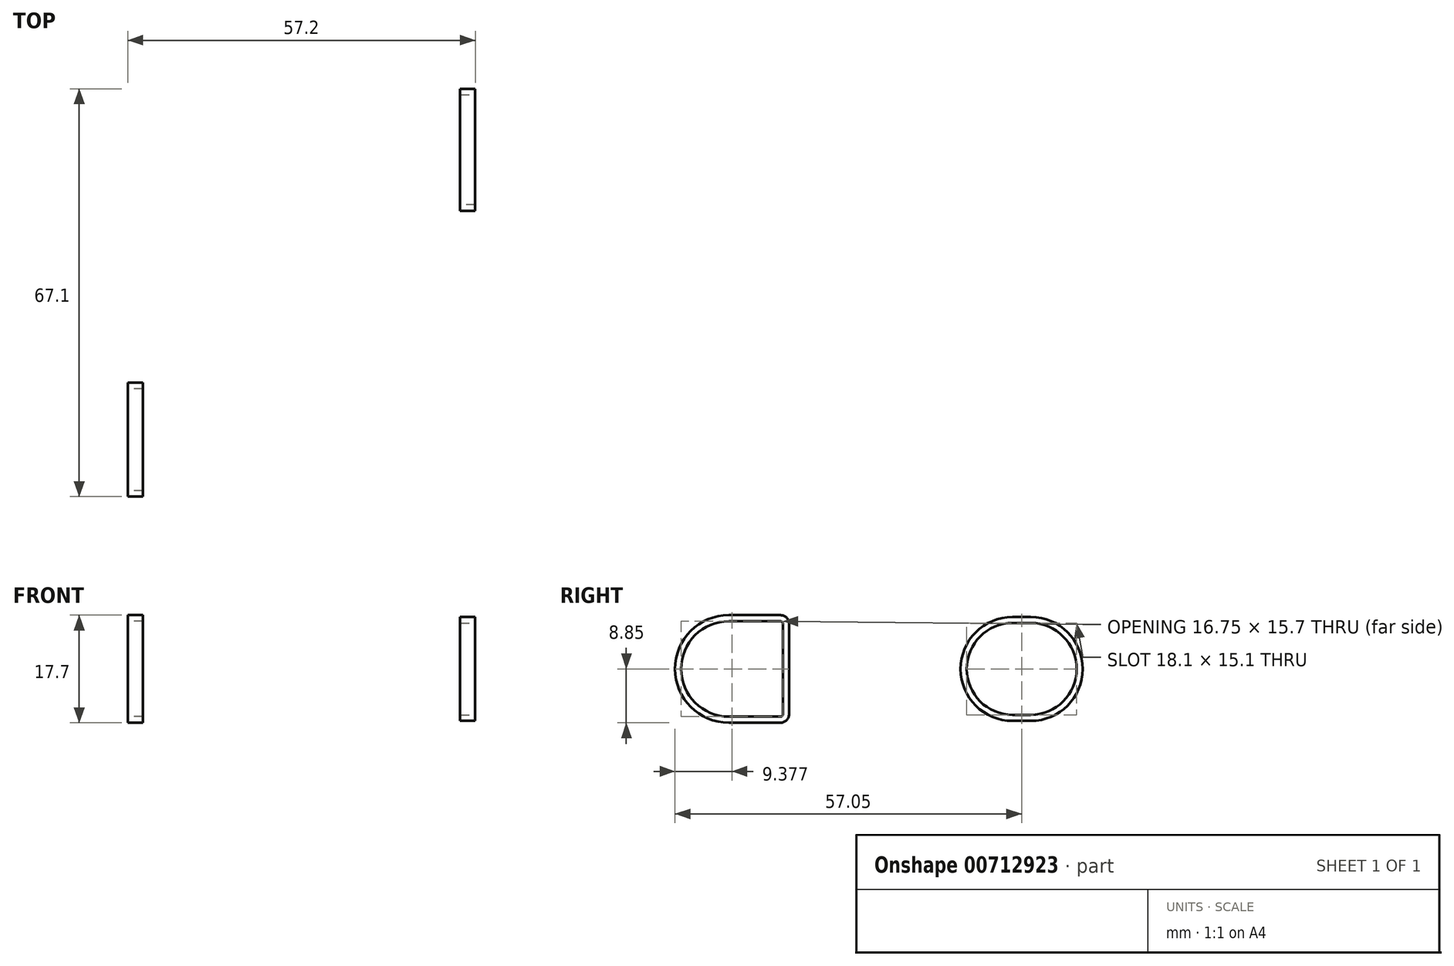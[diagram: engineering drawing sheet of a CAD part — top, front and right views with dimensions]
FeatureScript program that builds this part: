
annotation { "Feature Type Name" : "Feature", "Feature Type Description" : "" }
export const myFeature = defineFeature(function(context is Context, id is Id, definition is map)
    precondition{}
    {
        {
            var Q0;
            Q0=qCreatedBy(makeId("Front.planeOp"),FACE);
            var sketch = newSketch(context, id + "F0", { "sketchPlane" : qUnion([Q0])});
            skLineSegment(sketch, "E0", {"start": v(-11.53, 0) * mm, "end": v(14.53, 0) * mm});
            skLineSegment(sketch, "E1.bottom", {"start": v(-0.9, 8.55) * mm, "end": v(1.6, 8.55) * mm});
            skLineSegment(sketch, "E1.top", {"start": v(-0.9, 7.55) * mm, "end": v(1.6, 7.55) * mm});
            skLineSegment(sketch, "E1.left", {"start": v(-0.9, 8.55) * mm, "end": v(-0.9, 7.55) * mm});
            skLineSegment(sketch, "E1.right", {"start": v(1.6, 8.55) * mm, "end": v(1.6, 7.55) * mm});
            skSolve(sketch);
        }
        {
            var Q0;
            Q0=makeQuery(id+"F0.imprint","IMPRINT",FACE,{"disambiguationData":[TD([[makeQuery(id+"F0.imprint","IMPRINT",EDGE,{"derivedFrom":sQuery(id+"F0.wireOp",EDGE,"E1.bottom")}),-1.0]])]});
            extrude(context, id + "F1", {"entities" : qUnion([Q0]), "oppositeDirection" : true, "depth" : 3 * mm, "offsetDistance" : 25 * mm});
        }
        {
            var Q0;
            Q0=qCreatedBy(makeId("Right.planeOp"),FACE);
            var sketch = newSketch(context, id + "F2", { "sketchPlane" : qUnion([Q0])});
            skCircle(sketch, "E2", {"center": v(0, 0) * mm, "radius": 0.6 * mm});
            skSolve(sketch);
        }
        {
            var Q0;
            Q0 = qSketchRegion(id + "F2", true);
            extrude(context, id + "F3", {"entities" : qUnion([Q0]), "depth" : 25 * mm, "offsetDistance" : 25 * mm});
        }
        {
            var Q0;
            Q0=makeQuery(id+"F0.imprint","IMPRINT",FACE,{"disambiguationData":[TD([[makeQuery(id+"F0.imprint","IMPRINT",EDGE,{"derivedFrom":sQuery(id+"F0.wireOp",EDGE,"E1.bottom")}),-1.0]])]});
            var Q1;
            Q1=sQuery(id+"F0.wireOp",EDGE,"E0");
            revolve(context, id + "F4", {"operationType" : NewBodyOperationType.ADD, "surfaceOperationType" : NewSurfaceOperationType.NEW, "entities" : qUnion([Q0]), "axis" : qUnion([Q1]), "revolveType" : RevolveType.ONE_DIRECTION, "angle" : 180 * degree});
        }
        {
            var Q0;
            Q0=makeQuery(id+"F4.opRevolve","CAP_FACE",FACE,{"disambiguationData":[OSD([sQuery(id+"F0.wireOp",EDGE,"E1.bottom"),sQuery(id+"F0.wireOp",EDGE,"E1.top"),sQuery(id+"F0.wireOp",EDGE,"E1.left"),sQuery(id+"F0.wireOp",EDGE,"E1.right")])],"isStart":false});
            extrude(context, id + "F5", {"entities" : qUnion([Q0]), "operationType" : NewBodyOperationType.ADD, "depth" : 3 * mm, "offsetDistance" : 25 * mm});
        }
        {
            var Q0;
            Q0=makeQuery(id+"F3.opExtrude","SWEPT_BODY",BODY,{"disambiguationData":[OSD([sQuery(id+"F2.wireOp",EDGE,"E2")])]});
            deleteBodies(context, id + "F6", {"entities" : qUnion([Q0])});
        }
        {
            var Q0;
            Q0=makeQuery(id+"F1.opExtrude","CAP_FACE",FACE,{"disambiguationData":[OSD([sQuery(id+"F0.wireOp",EDGE,"E1.bottom"),sQuery(id+"F0.wireOp",EDGE,"E1.top"),sQuery(id+"F0.wireOp",EDGE,"E1.left"),sQuery(id+"F0.wireOp",EDGE,"E1.right")])],"isStart":false});
            cPlane(context, id + "F7", {"entities" : qUnion([Q0]), "cplaneType" : CPlaneType.OFFSET, "offset" : 0 * mm, "width" : 150 * mm, "height" : 150 * mm});
        }
        {
            var Q0;
            Q0=qCreatedBy(id+"F7.planeOp",FACE);
            var sketch = newSketch(context, id + "F8", { "sketchPlane" : qUnion([Q0])});
            skLineSegment(sketch, "E3", {"start": v(-8.27, 0) * mm, "end": v(9.97, 0) * mm});
            skSolve(sketch);
        }
        {
            var Q0;
            Q0=makeQuery(id+"F1.opExtrude","CAP_FACE",FACE,{"disambiguationData":[OSD([sQuery(id+"F0.wireOp",EDGE,"E1.bottom"),sQuery(id+"F0.wireOp",EDGE,"E1.top"),sQuery(id+"F0.wireOp",EDGE,"E1.left"),sQuery(id+"F0.wireOp",EDGE,"E1.right")])],"isStart":false});
            var Q1;
            Q1=sQuery(id+"F8.wireOp",EDGE,"E3");
            revolve(context, id + "F9", {"operationType" : NewBodyOperationType.ADD, "surfaceOperationType" : NewSurfaceOperationType.NEW, "entities" : qUnion([Q0]), "axis" : qUnion([Q1]), "revolveType" : RevolveType.ONE_DIRECTION, "angle" : 180 * degree});
        }
        {
            var Q0;
            Q0=makeQuery(id+"F1.opExtrude","SWEPT_BODY",BODY,{"disambiguationData":[OSD([sQuery(id+"F0.wireOp",EDGE,"E1.bottom"),sQuery(id+"F0.wireOp",EDGE,"E1.top"),sQuery(id+"F0.wireOp",EDGE,"E1.left"),sQuery(id+"F0.wireOp",EDGE,"E1.right")])]});
            transform(context, id + "F10", {"entities" : qUnion([Q0]), "transformType" : TransformType.TRANSLATION_3D, "dx" : 55.6 * mm, "dy" : 0 * mm, "dz" : 0 * mm, "makeCopy" : false});
        }
        {
            var Q0;
            Q0=makeQuery(id+"F1.opExtrude","SWEPT_BODY",BODY,{"disambiguationData":[OSD([sQuery(id+"F0.wireOp",EDGE,"E1.bottom"),sQuery(id+"F0.wireOp",EDGE,"E1.top"),sQuery(id+"F0.wireOp",EDGE,"E1.left"),sQuery(id+"F0.wireOp",EDGE,"E1.right")])]});
            transform(context, id + "F11", {"entities" : qUnion([Q0]), "transformType" : TransformType.TRANSLATION_3D, "dx" : 0 * mm, "dy" : 46.7 * mm, "dz" : 0 * mm, "makeCopy" : false});
        }
        {
            var Q0;
            Q0=qCreatedBy(makeId("Right.planeOp"),FACE);
            var sketch = newSketch(context, id + "F12", { "sketchPlane" : qUnion([Q0])});
            skCircle(sketch, "E4", {"center": v(0, 0) * mm, "radius": 7.5 * mm, "construction": true});
            skLineSegment(sketch, "E5.bottom", {"start": v(5.8, 7.75) * mm, "end": v(8.8, 7.75) * mm, "construction": true});
            skLineSegment(sketch, "E5.top", {"start": v(5.8, 4.75) * mm, "end": v(8.8, 4.75) * mm, "construction": true});
            skLineSegment(sketch, "E5.left", {"start": v(5.8, 7.75) * mm, "end": v(5.8, 4.75) * mm, "construction": true});
            skLineSegment(sketch, "E5.right", {"start": v(8.8, 7.75) * mm, "end": v(8.8, 4.75) * mm, "construction": true});
            skLineSegment(sketch, "E6", {"start": v(0, 0) * mm, "end": v(21.58, 0) * mm, "construction": true});
            skLineSegment(sketch, "E7.MirrorCS", {"start": v(5.8, -4.75) * mm, "end": v(8.8, -4.75) * mm, "construction": true});
            skLineSegment(sketch, "E8.MirrorCS", {"start": v(5.8, -7.75) * mm, "end": v(5.8, -4.75) * mm, "construction": true});
            skLineSegment(sketch, "E9.MirrorCS", {"start": v(5.8, -7.75) * mm, "end": v(8.8, -7.75) * mm, "construction": true});
            skLineSegment(sketch, "E10.MirrorCS", {"start": v(8.8, -7.75) * mm, "end": v(8.8, -4.75) * mm, "construction": true});
            skLineSegment(sketch, "E11", {"start": v(0, 7.85) * mm, "end": v(8.5, 7.85) * mm});
            skLineSegment(sketch, "E12", {"start": v(8.9, 7.45) * mm, "end": v(8.9, 0) * mm});
            skArc(sketch, "E13", {"start": v(0, 7.85) * mm, "mid": v(-5.55, 5.55) * mm, "end": v(-7.85, 0) * mm});
            skPoint(sketch, "E14.visualSharp", {"position": v(8.9, 7.85) * mm});
            skArc(sketch, "E14.filletArc", {"start": v(8.9, 7.45) * mm, "mid": v(8.79, 7.73) * mm, "end": v(8.5, 7.85) * mm});
            skArc(sketch, "E15.0", {"start": v(0, 8.85) * mm, "mid": v(-6.26, 6.26) * mm, "end": v(-8.85, 0) * mm});
            skLineSegment(sketch, "E15.1", {"start": v(0, 8.85) * mm, "end": v(8.5, 8.85) * mm});
            skArc(sketch, "E15.2", {"start": v(9.9, 7.45) * mm, "mid": v(9.5, 8.44) * mm, "end": v(8.5, 8.85) * mm});
            skLineSegment(sketch, "E15.3", {"start": v(9.9, 7.45) * mm, "end": v(9.9, 0) * mm});
            skArc(sketch, "E16.MirrorCS", {"start": v(8.9, -7.45) * mm, "mid": v(8.79, -7.73) * mm, "end": v(8.5, -7.85) * mm});
            skLineSegment(sketch, "E17.MirrorCS", {"start": v(8.9, -7.45) * mm, "end": v(8.9, 0) * mm});
            skLineSegment(sketch, "E18.MirrorCS", {"start": v(9.9, -7.45) * mm, "end": v(9.9, 0) * mm});
            skArc(sketch, "E19.MirrorCS", {"start": v(9.9, -7.45) * mm, "mid": v(9.5, -8.44) * mm, "end": v(8.5, -8.85) * mm});
            skLineSegment(sketch, "E20.MirrorCS", {"start": v(0, -7.85) * mm, "end": v(8.5, -7.85) * mm});
            skLineSegment(sketch, "E21.MirrorCS", {"start": v(0, -8.85) * mm, "end": v(8.5, -8.85) * mm});
            skArc(sketch, "E22.MirrorCS", {"start": v(0, -8.85) * mm, "mid": v(-6.26, -6.26) * mm, "end": v(-8.85, 0) * mm});
            skArc(sketch, "E23.MirrorCS", {"start": v(0, -7.85) * mm, "mid": v(-5.55, -5.55) * mm, "end": v(-7.85, 0) * mm});
            skSolve(sketch);
        }
        {
            var Q0;
            Q0=makeQuery(id+"F12.imprint","IMPRINT",FACE,{"disambiguationData":[TD([[makeQuery(id+"F12.imprint","IMPRINT",EDGE,{"derivedFrom":sQuery(id+"F12.wireOp",EDGE,"E11")}),1.0]])]});
            extrude(context, id + "F13", {"entities" : qUnion([Q0]), "depth" : 2.5 * mm, "offsetDistance" : 25 * mm});
        }
    });
